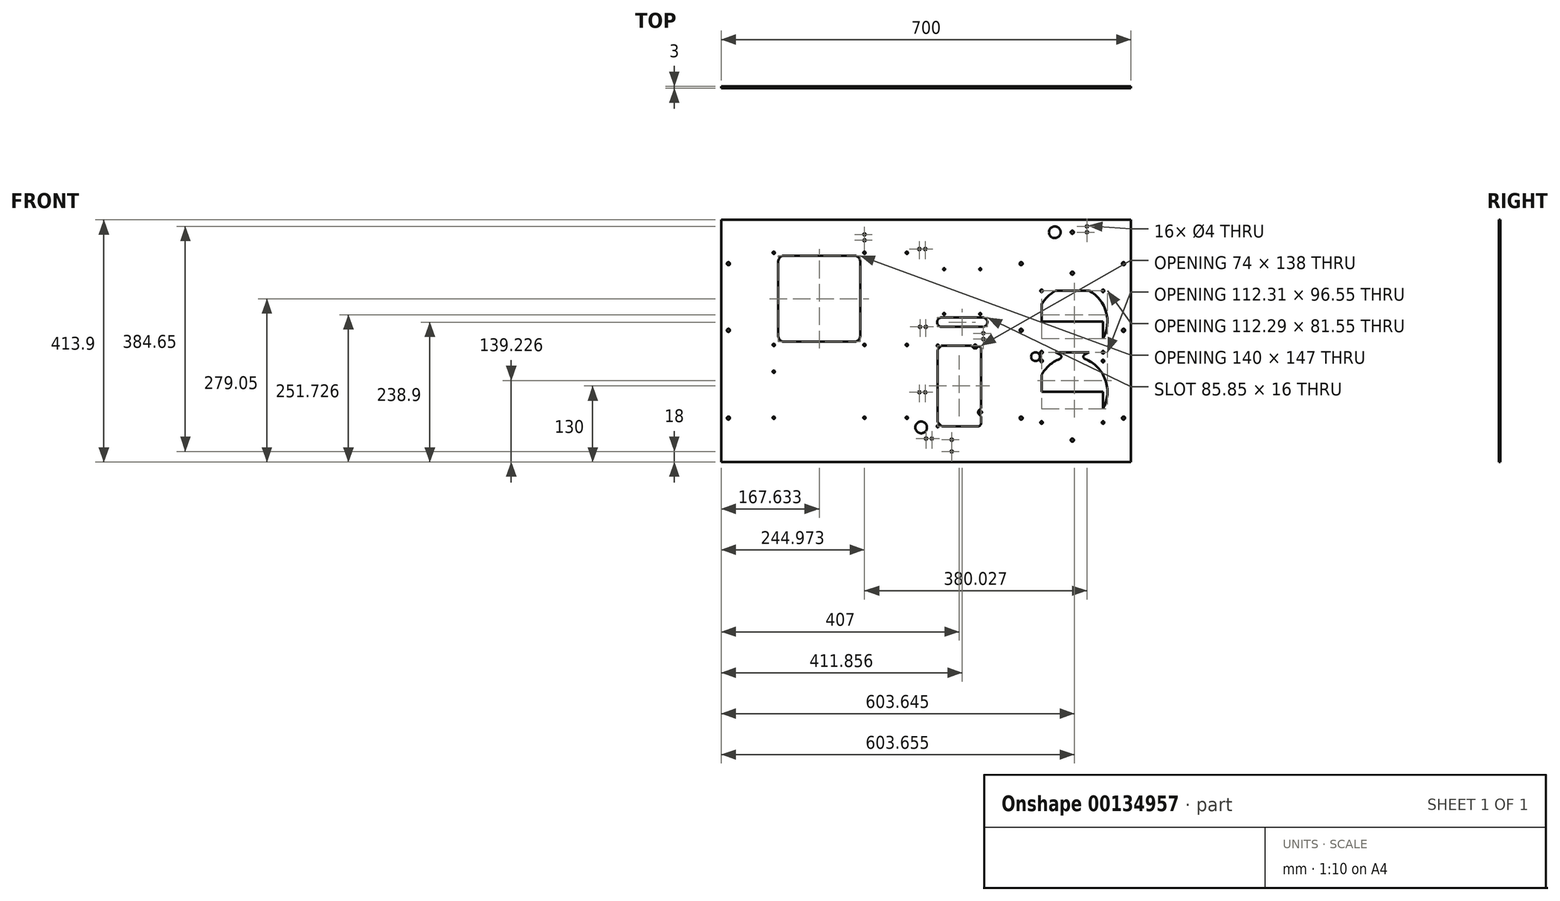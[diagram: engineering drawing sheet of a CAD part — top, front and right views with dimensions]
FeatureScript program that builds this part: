
annotation { "Feature Type Name" : "Feature", "Feature Type Description" : "" }
export const myFeature = defineFeature(function(context is Context, id is Id, definition is map)
    precondition{}
    {
        {
            var Q0;
            Q0=qCreatedBy(makeId("Front.planeOp"),FACE);
            var sketch = newSketch(context, id + "F0", { "sketchPlane" : qUnion([Q0])});
            skLineSegment(sketch, "E0.bottom", {"start": v(0, 0) * mm, "end": v(700, 0) * mm});
            skLineSegment(sketch, "E0.top", {"start": v(0, 413.9) * mm, "end": v(700, 413.9) * mm});
            skLineSegment(sketch, "E0.left", {"start": v(0, 0) * mm, "end": v(0, 413.9) * mm});
            skLineSegment(sketch, "E0.right", {"start": v(700, 0) * mm, "end": v(700, 413.9) * mm});
            skLineSegment(sketch, "E1", {"start": v(12.5, 0) * mm, "end": v(12.5, 413.9) * mm, "construction": true});
            skLineSegment(sketch, "E2", {"start": v(500, 413.9) * mm, "end": v(500, 0) * mm, "construction": true});
            skLineSegment(sketch, "E3", {"start": v(687.5, 413.9) * mm, "end": v(687.5, 0) * mm, "construction": true});
            skLineSegment(sketch, "E4", {"start": v(512.5, 413.9) * mm, "end": v(512.5, 0) * mm, "construction": true});
            skLineSegment(sketch, "E5", {"start": v(525, 413.9) * mm, "end": v(525, 0) * mm, "construction": true});
            skLineSegment(sketch, "E6.bottom", {"start": v(540, 60) * mm, "end": v(660, 60) * mm, "construction": true});
            skLineSegment(sketch, "E6.top", {"start": v(540, 180) * mm, "end": v(660, 180) * mm, "construction": true});
            skLineSegment(sketch, "E6.left", {"start": v(540, 60) * mm, "end": v(540, 180) * mm, "construction": true});
            skLineSegment(sketch, "E6.right", {"start": v(660, 60) * mm, "end": v(660, 180) * mm, "construction": true});
            skLineSegment(sketch, "E7", {"start": v(660, 180) * mm, "end": v(660, 300) * mm, "construction": true});
            skLineSegment(sketch, "E8", {"start": v(660, 300) * mm, "end": v(540, 300) * mm, "construction": true});
            skLineSegment(sketch, "E9", {"start": v(540, 300) * mm, "end": v(540, 180) * mm, "construction": true});
            skLineSegment(sketch, "E10", {"start": v(675, 413.9) * mm, "end": v(675, 0) * mm, "construction": true});
            skLineSegment(sketch, "E11", {"start": v(540, 60) * mm, "end": v(525, 60) * mm, "construction": true});
            skLineSegment(sketch, "E12", {"start": v(660, 60) * mm, "end": v(675, 60) * mm, "construction": true});
            skLineSegment(sketch, "E13.bottom", {"start": v(547.5, 292.5) * mm, "end": v(652.5, 292.5) * mm, "construction": true});
            skLineSegment(sketch, "E13.top", {"start": v(547.5, 187.5) * mm, "end": v(652.5, 187.5) * mm, "construction": true});
            skLineSegment(sketch, "E13.left", {"start": v(547.5, 292.5) * mm, "end": v(547.5, 187.5) * mm, "construction": true});
            skLineSegment(sketch, "E13.right", {"start": v(652.5, 292.5) * mm, "end": v(652.5, 187.5) * mm, "construction": true});
            skLineSegment(sketch, "E14.bottom", {"start": v(547.5, 172.5) * mm, "end": v(652.5, 172.5) * mm, "construction": true});
            skLineSegment(sketch, "E14.top", {"start": v(547.5, 67.5) * mm, "end": v(652.5, 67.5) * mm, "construction": true});
            skLineSegment(sketch, "E14.left", {"start": v(547.5, 172.5) * mm, "end": v(547.5, 67.5) * mm, "construction": true});
            skLineSegment(sketch, "E14.right", {"start": v(652.5, 172.5) * mm, "end": v(652.5, 67.5) * mm, "construction": true});
            skLineSegment(sketch, "E15", {"start": v(652.5, 67.5) * mm, "end": v(660, 67.5) * mm, "construction": true});
            skLineSegment(sketch, "E16", {"start": v(652.5, 67.5) * mm, "end": v(652.5, 60) * mm, "construction": true});
            skLineSegment(sketch, "E17", {"start": v(547.5, 172.5) * mm, "end": v(540, 172.5) * mm, "construction": true});
            skLineSegment(sketch, "E18", {"start": v(547.5, 172.5) * mm, "end": v(547.5, 180) * mm, "construction": true});
            skLineSegment(sketch, "E19", {"start": v(547.5, 187.5) * mm, "end": v(547.5, 180) * mm, "construction": true});
            skLineSegment(sketch, "E20", {"start": v(547.5, 187.5) * mm, "end": v(540, 187.5) * mm, "construction": true});
            skLineSegment(sketch, "E21", {"start": v(652.5, 292.5) * mm, "end": v(660, 292.5) * mm, "construction": true});
            skLineSegment(sketch, "E22", {"start": v(652.5, 292.5) * mm, "end": v(652.5, 300) * mm, "construction": true});
            skCircle(sketch, "E23", {"center": v(547.5, 292.5) * mm, "radius": 2.15 * mm});
            skCircle(sketch, "E24", {"center": v(652.5, 292.5) * mm, "radius": 2.15 * mm});
            skCircle(sketch, "E25", {"center": v(652.5, 187.5) * mm, "radius": 2.15 * mm});
            skCircle(sketch, "E26", {"center": v(547.5, 187.5) * mm, "radius": 2.15 * mm});
            skCircle(sketch, "E27", {"center": v(547.5, 172.5) * mm, "radius": 2.15 * mm});
            skCircle(sketch, "E28", {"center": v(652.5, 172.5) * mm, "radius": 2.15 * mm});
            skCircle(sketch, "E29", {"center": v(547.5, 67.5) * mm, "radius": 2.15 * mm});
            skCircle(sketch, "E30", {"center": v(652.5, 67.5) * mm, "radius": 2.15 * mm});
            skCircle(sketch, "E31", {"center": v(687.5, 338.9) * mm, "radius": 2.65 * mm});
            skCircle(sketch, "E32", {"center": v(687.5, 225) * mm, "radius": 2.65 * mm});
            skCircle(sketch, "E33", {"center": v(687.5, 75) * mm, "radius": 2.65 * mm});
            skCircle(sketch, "E34", {"center": v(512.5, 75) * mm, "radius": 2.65 * mm});
            skCircle(sketch, "E35", {"center": v(512.5, 225) * mm, "radius": 2.65 * mm});
            skCircle(sketch, "E36", {"center": v(512.5, 338.9) * mm, "radius": 2.65 * mm});
            skLineSegment(sketch, "E37", {"start": v(25, 413.9) * mm, "end": v(25, 0) * mm, "construction": true});
            skCircle(sketch, "E38", {"center": v(12.5, 75) * mm, "radius": 2.65 * mm});
            skCircle(sketch, "E39", {"center": v(12.5, 225) * mm, "radius": 2.65 * mm});
            skCircle(sketch, "E40", {"center": v(12.5, 338.9) * mm, "radius": 2.65 * mm});
            skLineSegment(sketch, "E41.bottom", {"start": v(80, 363.9) * mm, "end": v(323.71, 363.9) * mm, "construction": true});
            skLineSegment(sketch, "E41.top", {"start": v(80, 59.1) * mm, "end": v(323.71, 59.1) * mm, "construction": true});
            skLineSegment(sketch, "E41.left", {"start": v(80, 363.9) * mm, "end": v(80, 59.1) * mm, "construction": true});
            skLineSegment(sketch, "E41.right", {"start": v(323.71, 363.9) * mm, "end": v(323.71, 59.1) * mm, "construction": true});
            skLineSegment(sketch, "E42", {"start": v(323.71, 75.61) * mm, "end": v(80, 75.61) * mm, "construction": true});
            skLineSegment(sketch, "E43", {"start": v(80, 154.35) * mm, "end": v(323.71, 154.35) * mm, "construction": true});
            skLineSegment(sketch, "E44", {"start": v(80, 357.55) * mm, "end": v(323.71, 357.55) * mm, "construction": true});
            skLineSegment(sketch, "E45", {"start": v(317.36, 363.9) * mm, "end": v(317.36, 59.1) * mm, "construction": true});
            skLineSegment(sketch, "E46", {"start": v(244.97, 363.9) * mm, "end": v(244.97, 59.1) * mm, "construction": true});
            skLineSegment(sketch, "E47", {"start": v(323.71, 200.07) * mm, "end": v(80, 200.07) * mm, "construction": true});
            skLineSegment(sketch, "E48", {"start": v(90.03, 59.1) * mm, "end": v(90.03, 363.9) * mm, "construction": true});
            skPoint(sketch, "E49", {"position": v(90.03, 357.55) * mm});
            skPoint(sketch, "E50", {"position": v(244.97, 357.55) * mm});
            skPoint(sketch, "E51", {"position": v(317.36, 357.55) * mm});
            skPoint(sketch, "E52", {"position": v(317.36, 200.07) * mm});
            skPoint(sketch, "E53", {"position": v(244.97, 200.07) * mm});
            skPoint(sketch, "E54", {"position": v(90.03, 200.07) * mm});
            skPoint(sketch, "E55", {"position": v(90.03, 154.35) * mm});
            skPoint(sketch, "E56", {"position": v(244.97, 154.35) * mm});
            skPoint(sketch, "E57", {"position": v(317.36, 154.35) * mm});
            skPoint(sketch, "E58", {"position": v(90.03, 75.61) * mm});
            skPoint(sketch, "E59", {"position": v(244.97, 75.61) * mm});
            skPoint(sketch, "E60", {"position": v(317.36, 75.61) * mm});
            skCircle(sketch, "E61", {"center": v(90.03, 200.07) * mm, "radius": 1.98 * mm});
            skCircle(sketch, "E62", {"center": v(90.03, 154.35) * mm, "radius": 1.98 * mm});
            skCircle(sketch, "E63", {"center": v(90.03, 75.61) * mm, "radius": 1.98 * mm});
            skCircle(sketch, "E64", {"center": v(244.97, 75.61) * mm, "radius": 1.98 * mm});
            skCircle(sketch, "E65", {"center": v(317.36, 75.61) * mm, "radius": 1.98 * mm});
            skCircle(sketch, "E66", {"center": v(317.36, 200.07) * mm, "radius": 1.98 * mm});
            skCircle(sketch, "E67", {"center": v(244.97, 200.07) * mm, "radius": 1.98 * mm});
            skCircle(sketch, "E68", {"center": v(317.36, 357.55) * mm, "radius": 1.98 * mm});
            skCircle(sketch, "E69", {"center": v(244.97, 357.55) * mm, "radius": 1.98 * mm});
            skCircle(sketch, "E70", {"center": v(90.03, 357.55) * mm, "radius": 1.98 * mm});
            skLineSegment(sketch, "E71.bottom", {"start": v(364, 205) * mm, "end": v(450, 205) * mm, "construction": true});
            skLineSegment(sketch, "E71.top", {"start": v(364, 55) * mm, "end": v(450, 55) * mm, "construction": true});
            skLineSegment(sketch, "E71.left", {"start": v(364, 205) * mm, "end": v(364, 55) * mm, "construction": true});
            skLineSegment(sketch, "E71.right", {"start": v(450, 205) * mm, "end": v(450, 55) * mm, "construction": true});
            skLineSegment(sketch, "E72", {"start": v(364, 61) * mm, "end": v(370, 61) * mm});
            skLineSegment(sketch, "E73", {"start": v(364, 199) * mm, "end": v(370, 199) * mm});
            skLineSegment(sketch, "E74", {"start": v(450, 199) * mm, "end": v(434, 199) * mm});
            skLineSegment(sketch, "E75", {"start": v(450, 85) * mm, "end": v(444, 85) * mm});
            skCircle(sketch, "E76", {"center": v(444, 85) * mm, "radius": 1.75 * mm});
            skCircle(sketch, "E77", {"center": v(370, 61) * mm, "radius": 1.75 * mm});
            skCircle(sketch, "E78", {"center": v(370, 199) * mm, "radius": 1.75 * mm});
            skCircle(sketch, "E79", {"center": v(434, 199) * mm, "radius": 1.75 * mm});
            skLineSegment(sketch, "E80.bottom", {"start": v(376.93, 238.9) * mm, "end": v(446.78, 238.9) * mm, "construction": true});
            skLineSegment(sketch, "E80.top", {"start": v(376.93, 338.9) * mm, "end": v(446.78, 338.9) * mm, "construction": true});
            skLineSegment(sketch, "E80.left", {"start": v(376.93, 238.9) * mm, "end": v(376.93, 338.9) * mm, "construction": true});
            skLineSegment(sketch, "E80.right", {"start": v(446.78, 238.9) * mm, "end": v(446.78, 338.9) * mm, "construction": true});
            skLineSegment(sketch, "E81.bottom", {"start": v(381, 329.5) * mm, "end": v(442.72, 329.5) * mm, "construction": true});
            skLineSegment(sketch, "E81.top", {"start": v(381, 252.9) * mm, "end": v(442.72, 252.9) * mm, "construction": true});
            skLineSegment(sketch, "E81.left", {"start": v(381, 329.5) * mm, "end": v(381, 252.9) * mm, "construction": true});
            skLineSegment(sketch, "E81.right", {"start": v(442.72, 329.5) * mm, "end": v(442.72, 252.9) * mm, "construction": true});
            skLineSegment(sketch, "E82", {"start": v(381, 252.9) * mm, "end": v(376.93, 252.9) * mm, "construction": true});
            skLineSegment(sketch, "E83", {"start": v(381, 252.9) * mm, "end": v(381, 238.9) * mm, "construction": true});
            skLineSegment(sketch, "E84", {"start": v(442.72, 329.5) * mm, "end": v(442.72, 338.9) * mm, "construction": true});
            skLineSegment(sketch, "E85", {"start": v(442.72, 329.5) * mm, "end": v(446.78, 329.5) * mm, "construction": true});
            skLineSegment(sketch, "E86", {"start": v(376.93, 238.9) * mm, "end": v(323.71, 238.9) * mm});
            skLineSegment(sketch, "E87", {"start": v(446.78, 238.9) * mm, "end": v(500, 238.9) * mm});
            skCircle(sketch, "E88", {"center": v(381, 329.5) * mm, "radius": 1.65 * mm});
            skCircle(sketch, "E89", {"center": v(442.72, 329.5) * mm, "radius": 1.65 * mm});
            skCircle(sketch, "E90", {"center": v(442.72, 252.9) * mm, "radius": 1.65 * mm});
            skCircle(sketch, "E91", {"center": v(381, 252.9) * mm, "radius": 1.65 * mm});
            skCircle(sketch, "E92", {"center": v(446.78, 238.9) * mm, "radius": 8 * mm});
            skPoint(sketch, "E93.startSnap0", {"position": v(381, 245.9) * mm});
            skCircle(sketch, "E94", {"center": v(376.93, 238.9) * mm, "radius": 8 * mm});
            skLineSegment(sketch, "E95", {"start": v(376.93, 246.9) * mm, "end": v(446.78, 246.9) * mm});
            skLineSegment(sketch, "E96", {"start": v(446.78, 230.9) * mm, "end": v(376.93, 230.9) * mm});
            skCircle(sketch, "E97", {"center": v(370, 199) * mm, "radius": 5 * mm});
            skCircle(sketch, "E98", {"center": v(434, 199) * mm, "radius": 5 * mm});
            skCircle(sketch, "E99", {"center": v(370, 61) * mm, "radius": 5 * mm});
            skCircle(sketch, "E100", {"center": v(444, 85) * mm, "radius": 5 * mm});
            skLineSegment(sketch, "E101", {"start": v(370, 199) * mm, "end": v(434, 199) * mm});
            skLineSegment(sketch, "E102", {"start": v(444, 199) * mm, "end": v(444, 85) * mm});
            skLineSegment(sketch, "E103", {"start": v(444, 85) * mm, "end": v(444, 61) * mm});
            skLineSegment(sketch, "E104", {"start": v(444, 61) * mm, "end": v(370, 61) * mm});
            skLineSegment(sketch, "E105", {"start": v(370, 61) * mm, "end": v(370, 199) * mm});
            skLineSegment(sketch, "E106.bottom", {"start": v(107.63, 352.55) * mm, "end": v(227.63, 352.55) * mm});
            skLineSegment(sketch, "E106.top", {"start": v(107.63, 205.55) * mm, "end": v(227.63, 205.55) * mm});
            skLineSegment(sketch, "E106.left", {"start": v(97.63, 342.55) * mm, "end": v(97.63, 215.55) * mm});
            skLineSegment(sketch, "E106.right", {"start": v(237.63, 342.55) * mm, "end": v(237.63, 215.55) * mm});
            skPoint(sketch, "E107.visualSharp", {"position": v(97.63, 352.55) * mm});
            skArc(sketch, "E107.filletArc", {"start": v(107.63, 352.55) * mm, "mid": v(100.56, 349.62) * mm, "end": v(97.63, 342.55) * mm});
            skPoint(sketch, "E108.visualSharp", {"position": v(97.63, 205.55) * mm});
            skArc(sketch, "E108.filletArc", {"start": v(97.63, 215.55) * mm, "mid": v(100.56, 208.48) * mm, "end": v(107.63, 205.55) * mm});
            skPoint(sketch, "E109.visualSharp", {"position": v(237.63, 205.55) * mm});
            skArc(sketch, "E109.filletArc", {"start": v(227.63, 205.55) * mm, "mid": v(234.7, 208.48) * mm, "end": v(237.63, 215.55) * mm});
            skPoint(sketch, "E110.visualSharp", {"position": v(237.63, 352.55) * mm});
            skArc(sketch, "E110.filletArc", {"start": v(237.63, 342.55) * mm, "mid": v(234.7, 349.62) * mm, "end": v(227.63, 352.55) * mm});
            skCircle(sketch, "E111", {"center": v(338.71, 119.1) * mm, "radius": 2 * mm});
            skCircle(sketch, "E112", {"center": v(348.71, 119.1) * mm, "radius": 2 * mm});
            skLineSegment(sketch, "E113", {"start": v(338.71, 119.1) * mm, "end": v(348.71, 119.1) * mm});
            skCircle(sketch, "E114", {"center": v(341.71, 59.1) * mm, "radius": 10 * mm});
            skCircle(sketch, "E115", {"center": v(350, 40) * mm, "radius": 2 * mm});
            skLineSegment(sketch, "E116", {"start": v(350, 40) * mm, "end": v(360, 40) * mm});
            skCircle(sketch, "E117", {"center": v(360, 40) * mm, "radius": 2 * mm});
            skLineSegment(sketch, "E118", {"start": v(547.5, 120) * mm, "end": v(652.5, 120) * mm});
            skCircle(sketch, "E119", {"center": v(600, 120) * mm, "radius": 60 * mm});
            skLineSegment(sketch, "E120", {"start": v(547.5, 240) * mm, "end": v(652.5, 240) * mm});
            skCircle(sketch, "E121", {"center": v(600, 240) * mm, "radius": 60 * mm});
            skLineSegment(sketch, "E122", {"start": v(547.5, 269.05) * mm, "end": v(547.5, 210.95) * mm});
            skLineSegment(sketch, "E123", {"start": v(570.95, 187.5) * mm, "end": v(629.05, 187.5) * mm});
            skLineSegment(sketch, "E124", {"start": v(570.95, 292.5) * mm, "end": v(629.05, 292.5) * mm});
            skLineSegment(sketch, "E125", {"start": v(652.5, 269.05) * mm, "end": v(652.5, 210.95) * mm});
            skLineSegment(sketch, "E126", {"start": v(570.95, 172.5) * mm, "end": v(629.05, 172.5) * mm});
            skLineSegment(sketch, "E127", {"start": v(652.5, 149.05) * mm, "end": v(652.5, 90.95) * mm});
            skLineSegment(sketch, "E128", {"start": v(629.05, 67.5) * mm, "end": v(570.95, 67.5) * mm});
            skLineSegment(sketch, "E129", {"start": v(547.5, 90.95) * mm, "end": v(547.5, 149.05) * mm});
            skCircle(sketch, "E130", {"center": v(339.71, 230.9) * mm, "radius": 2 * mm});
            skCircle(sketch, "E131", {"center": v(349.71, 230.9) * mm, "radius": 2 * mm});
            skLineSegment(sketch, "E132", {"start": v(339.71, 230.9) * mm, "end": v(349.71, 230.9) * mm});
            skCircle(sketch, "E133", {"center": v(338.71, 363.9) * mm, "radius": 2 * mm});
            skCircle(sketch, "E134", {"center": v(348.71, 363.9) * mm, "radius": 2 * mm});
            skLineSegment(sketch, "E135", {"start": v(338.71, 363.9) * mm, "end": v(348.71, 363.9) * mm});
            skCircle(sketch, "E136", {"center": v(244.97, 378.9) * mm, "radius": 2 * mm});
            skCircle(sketch, "E137", {"center": v(244.97, 388.9) * mm, "radius": 2 * mm});
            skLineSegment(sketch, "E138", {"start": v(244.97, 378.9) * mm, "end": v(244.97, 388.9) * mm});
            skCircle(sketch, "E139", {"center": v(448, 220) * mm, "radius": 2 * mm});
            skCircle(sketch, "E140", {"center": v(448, 210) * mm, "radius": 2 * mm});
            skLineSegment(sketch, "E141", {"start": v(448, 220) * mm, "end": v(448, 210) * mm});
            skLineSegment(sketch, "E142", {"start": v(581.27, 183) * mm, "end": v(581.27, 177) * mm});
            skLineSegment(sketch, "E143", {"start": v(618.73, 183) * mm, "end": v(618.73, 177) * mm});
            skLineSegment(sketch, "E144", {"start": v(600, 300) * mm, "end": v(600, 322.65) * mm});
            skCircle(sketch, "E145", {"center": v(600, 322.65) * mm, "radius": 2.65 * mm});
            skLineSegment(sketch, "E146", {"start": v(600, 60) * mm, "end": v(600, 37.35) * mm});
            skCircle(sketch, "E147", {"center": v(600, 37.35) * mm, "radius": 2.65 * mm});
            skCircle(sketch, "E148", {"center": v(394, 38) * mm, "radius": 2 * mm});
            skCircle(sketch, "E149", {"center": v(394, 18) * mm, "radius": 2 * mm});
            skLineSegment(sketch, "E150", {"start": v(394, 38) * mm, "end": v(394, 18) * mm});
            skCircle(sketch, "E151", {"center": v(600, 392.65) * mm, "radius": 2.65 * mm});
            skCircle(sketch, "E152", {"center": v(625, 392.65) * mm, "radius": 2 * mm});
            skCircle(sketch, "E153", {"center": v(625, 402.65) * mm, "radius": 2 * mm});
            skLineSegment(sketch, "E154", {"start": v(625, 392.65) * mm, "end": v(625, 402.65) * mm});
            skCircle(sketch, "E155", {"center": v(570, 392.65) * mm, "radius": 10 * mm});
            skCircle(sketch, "E156", {"center": v(537, 180) * mm, "radius": 7.5 * mm});
            skSolve(sketch);
        }
        {
            var Q0;
            Q0=makeQuery(id+"F0.imprint","IMPRINT",FACE,{"disambiguationData":[TD([[makeQuery(id+"F0.imprint","IMPRINT",EDGE,{"derivedFrom":sQuery(id+"F0.wireOp",EDGE,"E0.bottom")}),1.0]])]});
            var Q1;
            {var subQ0=sQuery(id+"F0.wireOp",EDGE,"E101");var subQ1=sQuery(id+"F0.wireOp",EDGE,"E78");var subQ2=makeQuery(id+"F0.imprint","INTERSECT",VERTEX,{"derivedFrom":[subQ1,subQ0]});Q1=makeQuery(id+"F0.imprint","IMPRINT",FACE,{"disambiguationData":[TD([[makeQuery(id+"F0.imprint","IMPRINT",EDGE,{"disambiguationData":[TD([[subQ2,1.0]])],"derivedFrom":subQ1}),-1.0]])]});}
            var Q2;
            {var subQ0=sQuery(id+"F0.wireOp",EDGE,"E97");var subQ1=sQuery(id+"F0.wireOp",EDGE,"E73");var subQ2=makeQuery(id+"F0.imprint","INTERSECT",VERTEX,{"derivedFrom":[subQ1,subQ0]});Q2=makeQuery(id+"F0.imprint","IMPRINT",FACE,{"disambiguationData":[TD([[makeQuery(id+"F0.imprint","IMPRINT",EDGE,{"disambiguationData":[TD([[subQ2,-1.0]])],"derivedFrom":subQ1}),-1.0]])]});}
            var Q3;
            {var subQ0=sQuery(id+"F0.wireOp",EDGE,"E97");var subQ1=sQuery(id+"F0.wireOp",EDGE,"E73");var subQ2=makeQuery(id+"F0.imprint","INTERSECT",VERTEX,{"derivedFrom":[subQ1,subQ0]});Q3=makeQuery(id+"F0.imprint","IMPRINT",FACE,{"disambiguationData":[TD([[makeQuery(id+"F0.imprint","IMPRINT",EDGE,{"disambiguationData":[TD([[subQ2,-1.0]])],"derivedFrom":subQ1}),1.0]])]});}
            var Q4;
            {var subQ0=sQuery(id+"F0.wireOp",EDGE,"E98");var subQ1=sQuery(id+"F0.wireOp",EDGE,"E74");var subQ2=makeQuery(id+"F0.imprint","INTERSECT",VERTEX,{"derivedFrom":[subQ1,subQ0]});Q4=makeQuery(id+"F0.imprint","IMPRINT",FACE,{"disambiguationData":[TD([[makeQuery(id+"F0.imprint","IMPRINT",EDGE,{"disambiguationData":[TD([[subQ2,-1.0]])],"derivedFrom":subQ1}),1.0]])]});}
            var Q5;
            {var subQ0=sQuery(id+"F0.wireOp",EDGE,"E98");var subQ1=sQuery(id+"F0.wireOp",EDGE,"E74");var subQ2=makeQuery(id+"F0.imprint","INTERSECT",VERTEX,{"derivedFrom":[subQ1,subQ0]});Q5=makeQuery(id+"F0.imprint","IMPRINT",FACE,{"disambiguationData":[TD([[makeQuery(id+"F0.imprint","IMPRINT",EDGE,{"disambiguationData":[TD([[subQ2,-1.0]])],"derivedFrom":subQ1}),-1.0]])]});}
            var Q6;
            {var subQ0=sQuery(id+"F0.wireOp",EDGE,"E105");var subQ1=sQuery(id+"F0.wireOp",EDGE,"E77");var subQ2=makeQuery(id+"F0.imprint","INTERSECT",VERTEX,{"derivedFrom":[subQ1,subQ0]});Q6=makeQuery(id+"F0.imprint","IMPRINT",FACE,{"disambiguationData":[TD([[makeQuery(id+"F0.imprint","IMPRINT",EDGE,{"disambiguationData":[TD([[subQ2,1.0]])],"derivedFrom":subQ1}),-1.0]])]});}
            var Q7;
            {var subQ0=sQuery(id+"F0.wireOp",EDGE,"E99");var subQ1=sQuery(id+"F0.wireOp",EDGE,"E72");var subQ2=makeQuery(id+"F0.imprint","INTERSECT",VERTEX,{"derivedFrom":[subQ1,subQ0]});Q7=makeQuery(id+"F0.imprint","IMPRINT",FACE,{"disambiguationData":[TD([[makeQuery(id+"F0.imprint","IMPRINT",EDGE,{"disambiguationData":[TD([[subQ2,-1.0]])],"derivedFrom":subQ1}),-1.0]])]});}
            var Q8;
            {var subQ0=sQuery(id+"F0.wireOp",EDGE,"E99");var subQ1=sQuery(id+"F0.wireOp",EDGE,"E72");var subQ2=makeQuery(id+"F0.imprint","INTERSECT",VERTEX,{"derivedFrom":[subQ1,subQ0]});Q8=makeQuery(id+"F0.imprint","IMPRINT",FACE,{"disambiguationData":[TD([[makeQuery(id+"F0.imprint","IMPRINT",EDGE,{"disambiguationData":[TD([[subQ2,-1.0]])],"derivedFrom":subQ1}),1.0]])]});}
            var Q9;
            {var subQ0=sQuery(id+"F0.wireOp",EDGE,"E100");var subQ1=sQuery(id+"F0.wireOp",EDGE,"E75");var subQ2=makeQuery(id+"F0.imprint","INTERSECT",VERTEX,{"derivedFrom":[subQ1,subQ0]});Q9=makeQuery(id+"F0.imprint","IMPRINT",FACE,{"disambiguationData":[TD([[makeQuery(id+"F0.imprint","IMPRINT",EDGE,{"disambiguationData":[TD([[subQ2,-1.0]])],"derivedFrom":subQ1}),1.0]])]});}
            var Q10;
            {var subQ0=sQuery(id+"F0.wireOp",EDGE,"E102");var subQ1=sQuery(id+"F0.wireOp",EDGE,"E76");var subQ2=makeQuery(id+"F0.imprint","INTERSECT",VERTEX,{"derivedFrom":[subQ1,subQ0]});Q10=makeQuery(id+"F0.imprint","IMPRINT",FACE,{"disambiguationData":[TD([[makeQuery(id+"F0.imprint","IMPRINT",EDGE,{"disambiguationData":[TD([[subQ2,-1.0]])],"derivedFrom":subQ1}),-1.0]])]});}
            var Q11;
            {var subQ0=sQuery(id+"F0.wireOp",EDGE,"E100");var subQ1=sQuery(id+"F0.wireOp",EDGE,"E75");var subQ2=makeQuery(id+"F0.imprint","INTERSECT",VERTEX,{"derivedFrom":[subQ1,subQ0]});Q11=makeQuery(id+"F0.imprint","IMPRINT",FACE,{"disambiguationData":[TD([[makeQuery(id+"F0.imprint","IMPRINT",EDGE,{"disambiguationData":[TD([[subQ2,-1.0]])],"derivedFrom":subQ1}),-1.0]])]});}
            var Q12;
            {var subQ0=sQuery(id+"F0.wireOp",EDGE,"E122");var subQ1=sQuery(id+"F0.wireOp",EDGE,"E121");var subQ2=makeQuery(id+"F0.imprint","INTERSECT",VERTEX,{"disambiguationData":[OD(0.0)],"derivedFrom":[subQ1,subQ0]});Q12=makeQuery(id+"F0.imprint","IMPRINT",FACE,{"disambiguationData":[TD([[makeQuery(id+"F0.imprint","IMPRINT",EDGE,{"disambiguationData":[TD([[subQ2,-1.0]])],"derivedFrom":subQ1}),1.0]])]});}
            var Q13;
            {var subQ0=sQuery(id+"F0.wireOp",EDGE,"E125");var subQ1=sQuery(id+"F0.wireOp",EDGE,"E121");var subQ2=makeQuery(id+"F0.imprint","INTERSECT",VERTEX,{"disambiguationData":[OD(0.0)],"derivedFrom":[subQ1,subQ0]});Q13=makeQuery(id+"F0.imprint","IMPRINT",FACE,{"disambiguationData":[TD([[makeQuery(id+"F0.imprint","IMPRINT",EDGE,{"disambiguationData":[TD([[subQ2,1.0]])],"derivedFrom":subQ1}),1.0]])]});}
            var Q14;
            {var subQ0=sQuery(id+"F0.wireOp",EDGE,"E124");Q14=makeQuery(id+"F0.imprint","IMPRINT",FACE,{"disambiguationData":[TD([[makeQuery(id+"F0.imprint","IMPRINT",EDGE,{"derivedFrom":subQ0}),1.0]])]});}
            var Q15;
            {var subQ0=sQuery(id+"F0.wireOp",EDGE,"E129");var subQ1=sQuery(id+"F0.wireOp",EDGE,"E119");var subQ2=makeQuery(id+"F0.imprint","INTERSECT",VERTEX,{"disambiguationData":[OD(0.0)],"derivedFrom":[subQ1,subQ0]});Q15=makeQuery(id+"F0.imprint","IMPRINT",FACE,{"disambiguationData":[TD([[makeQuery(id+"F0.imprint","IMPRINT",EDGE,{"disambiguationData":[TD([[subQ2,1.0]])],"derivedFrom":subQ1}),1.0]])]});}
            var Q16;
            {var subQ0=sQuery(id+"F0.wireOp",EDGE,"E128");Q16=makeQuery(id+"F0.imprint","IMPRINT",FACE,{"disambiguationData":[TD([[makeQuery(id+"F0.imprint","IMPRINT",EDGE,{"derivedFrom":subQ0}),1.0]])]});}
            var Q17;
            {var subQ0=sQuery(id+"F0.wireOp",EDGE,"E127");var subQ1=sQuery(id+"F0.wireOp",EDGE,"E119");var subQ2=makeQuery(id+"F0.imprint","INTERSECT",VERTEX,{"disambiguationData":[OD(0.0)],"derivedFrom":[subQ1,subQ0]});Q17=makeQuery(id+"F0.imprint","IMPRINT",FACE,{"disambiguationData":[TD([[makeQuery(id+"F0.imprint","IMPRINT",EDGE,{"disambiguationData":[TD([[subQ2,1.0]])],"derivedFrom":subQ1}),1.0]])]});}
            extrude(context, id + "F1", {"entities" : qUnion([Q0, Q1, Q2, Q3, Q4, Q5, Q6, Q7, Q8, Q9, Q10, Q11, Q12, Q13, Q14, Q15, Q16, Q17]), "depth" : 3 * mm});
        }
        {
            var Q0;
            Q0=makeQuery(id+"F1.opExtrude","SWEPT_EDGE",EDGE,{"disambiguationData":[OSD([sQuery(id+"F0.wireOp",EDGE,"E74"),sQuery(id+"F0.wireOp",EDGE,"E102")])]});
            var Q1;
            Q1=makeQuery(id+"F1.opExtrude","SWEPT_EDGE",EDGE,{"disambiguationData":[OSD([sQuery(id+"F0.wireOp",EDGE,"E74"),sQuery(id+"F0.wireOp",EDGE,"E98")])]});
            fillet(context, id + "F2", {"entities" : qUnion([Q0, Q1]), "radius" : 5.63 * mm, "tangentPropagation" : true, "allowEdgeOverflow" : false});
        }
        {
            var Q0;
            {var subQ0=sQuery(id+"F0.wireOp",EDGE,"E74");Q0=makeQuery(id+"F2.opFillet","BLEND_EDGE",EDGE,{"blendedFrom":[makeQuery(id+"F1.opExtrude","SWEPT_EDGE",EDGE,{"disambiguationData":[OSD([subQ0,sQuery(id+"F0.wireOp",EDGE,"E102")])]}),makeQuery(id+"F1.opExtrude","SWEPT_EDGE",EDGE,{"disambiguationData":[OSD([subQ0,sQuery(id+"F0.wireOp",EDGE,"E98")])]})],"blendedInto":[]});}
            fillet(context, id + "F3", {"entities" : qUnion([Q0]), "radius" : 3.07 * mm, "tangentPropagation" : true, "allowEdgeOverflow" : false});
        }
        {
            var Q0;
            Q0=makeQuery(id+"F1.opExtrude","SWEPT_EDGE",EDGE,{"disambiguationData":[OSD([sQuery(id+"F0.wireOp",EDGE,"E98"),sQuery(id+"F0.wireOp",EDGE,"E101")])]});
            fillet(context, id + "F4", {"entities" : qUnion([Q0]), "radius" : 5 * mm, "tangentPropagation" : true, "allowEdgeOverflow" : false});
        }
        {
            var Q0;
            Q0=makeQuery(id+"F1.opExtrude","SWEPT_EDGE",EDGE,{"disambiguationData":[OSD([sQuery(id+"F0.wireOp",EDGE,"E97"),sQuery(id+"F0.wireOp",EDGE,"E101")])]});
            var Q1;
            Q1=makeQuery(id+"F1.opExtrude","SWEPT_EDGE",EDGE,{"disambiguationData":[OSD([sQuery(id+"F0.wireOp",EDGE,"E97"),sQuery(id+"F0.wireOp",EDGE,"E105")])]});
            var Q2;
            Q2=makeQuery(id+"F1.opExtrude","SWEPT_EDGE",EDGE,{"disambiguationData":[OSD([sQuery(id+"F0.wireOp",EDGE,"E99"),sQuery(id+"F0.wireOp",EDGE,"E104")])]});
            var Q3;
            Q3=makeQuery(id+"F1.opExtrude","SWEPT_EDGE",EDGE,{"disambiguationData":[OSD([sQuery(id+"F0.wireOp",EDGE,"E99"),sQuery(id+"F0.wireOp",EDGE,"E105")])]});
            var Q4;
            Q4=makeQuery(id+"F1.opExtrude","SWEPT_EDGE",EDGE,{"disambiguationData":[OSD([sQuery(id+"F0.wireOp",EDGE,"E100"),sQuery(id+"F0.wireOp",EDGE,"E103")])]});
            var Q5;
            Q5=makeQuery(id+"F1.opExtrude","SWEPT_EDGE",EDGE,{"disambiguationData":[OSD([sQuery(id+"F0.wireOp",EDGE,"E100"),sQuery(id+"F0.wireOp",EDGE,"E102")])]});
            var Q6;
            Q6=makeQuery(id+"F1.opExtrude","SWEPT_EDGE",EDGE,{"disambiguationData":[OSD([sQuery(id+"F0.wireOp",EDGE,"E103"),sQuery(id+"F0.wireOp",EDGE,"E104")])]});
            fillet(context, id + "F5", {"entities" : qUnion([Q0, Q1, Q2, Q3, Q4, Q5, Q6]), "radius" : 5 * mm, "tangentPropagation" : true, "allowEdgeOverflow" : false});
        }
        {
            var Q0;
            Q0=makeQuery(id+"F1.opExtrude","SWEPT_EDGE",EDGE,{"disambiguationData":[OSD([sQuery(id+"F0.wireOp",EDGE,"E119"),sQuery(id+"F0.wireOp",EDGE,"E142")])]});
            var Q1;
            Q1=makeQuery(id+"F1.opExtrude","SWEPT_EDGE",EDGE,{"disambiguationData":[OSD([sQuery(id+"F0.wireOp",EDGE,"E121"),sQuery(id+"F0.wireOp",EDGE,"E142")])]});
            var Q2;
            Q2=makeQuery(id+"F1.opExtrude","SWEPT_EDGE",EDGE,{"disambiguationData":[OSD([sQuery(id+"F0.wireOp",EDGE,"E121"),sQuery(id+"F0.wireOp",EDGE,"E143")])]});
            var Q3;
            Q3=makeQuery(id+"F1.opExtrude","SWEPT_EDGE",EDGE,{"disambiguationData":[OSD([sQuery(id+"F0.wireOp",EDGE,"E119"),sQuery(id+"F0.wireOp",EDGE,"E143")])]});
            fillet(context, id + "F6", {"entities" : qUnion([Q0, Q1, Q2, Q3]), "radius" : 5 * mm, "tangentPropagation" : true, "allowEdgeOverflow" : false});
        }
    });
